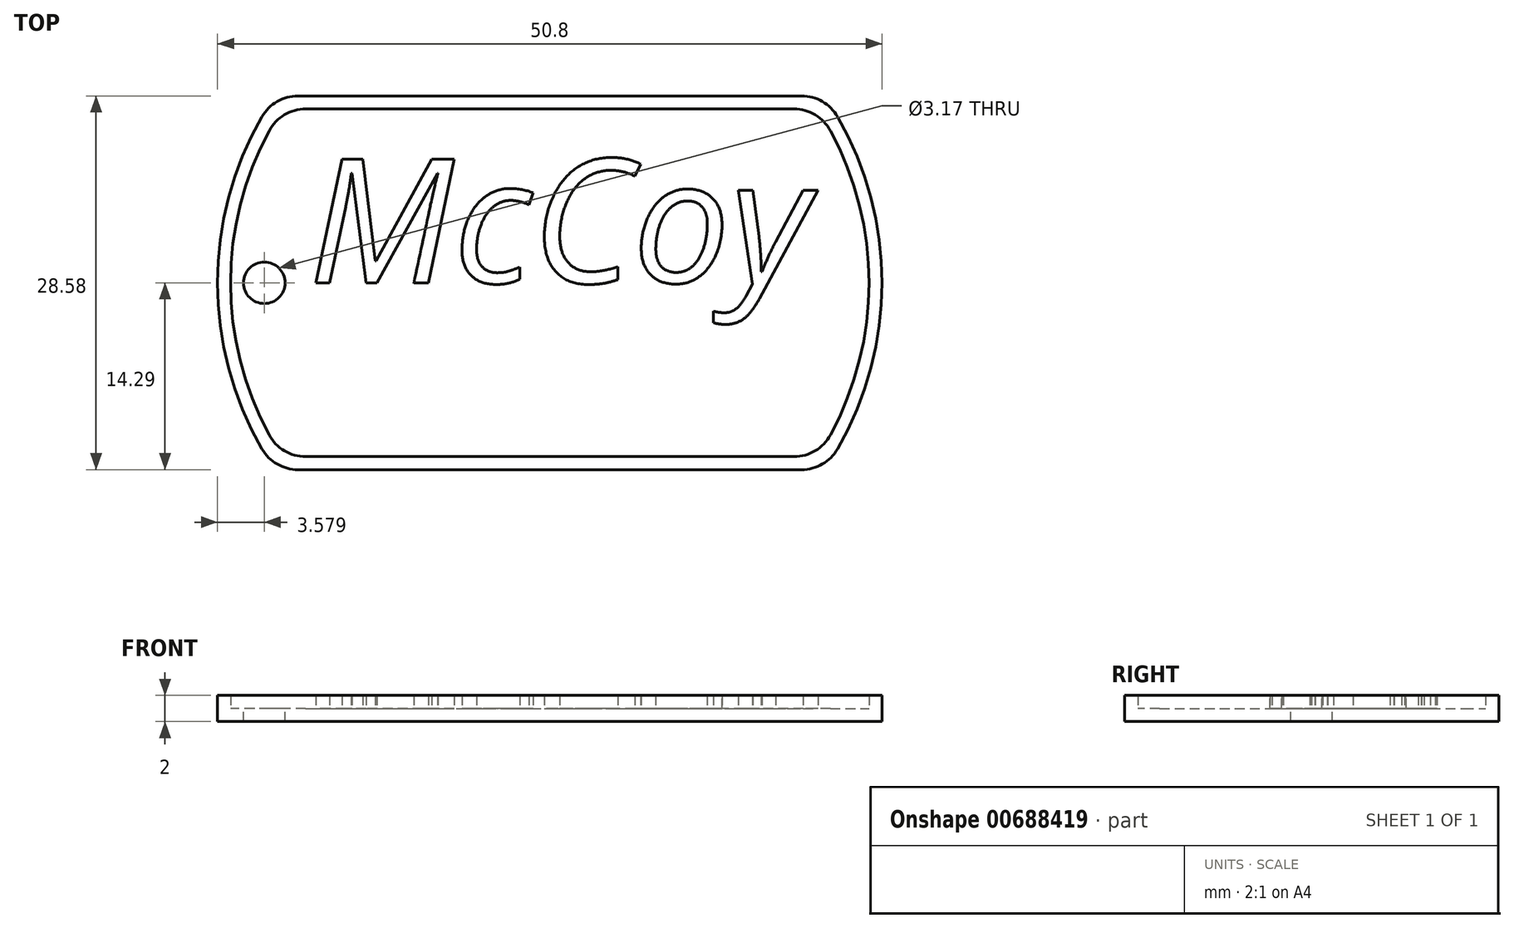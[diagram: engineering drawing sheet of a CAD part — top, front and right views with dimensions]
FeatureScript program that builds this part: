
annotation { "Feature Type Name" : "Feature", "Feature Type Description" : "" }
export const myFeature = defineFeature(function(context is Context, id is Id, definition is map)
    precondition{}
    {
        {
            var Q0;
            Q0=qCreatedBy(makeId("Top.planeOp"),FACE);
            var sketch = newSketch(context, id + "F0", { "sketchPlane" : qUnion([Q0])});
            skArc(sketch, "E0", {"start": v(-22, 12.7) * mm, "mid": v(-25.4, 0) * mm, "end": v(-22, -12.7) * mm});
            skLineSegment(sketch, "E1.top", {"start": v(-19.25, -14.29) * mm, "end": v(19.25, -14.29) * mm});
            skArc(sketch, "E2.trimOffspring", {"start": v(22, -12.7) * mm, "mid": v(25.4, 0) * mm, "end": v(22, 12.7) * mm});
            skLineSegment(sketch, "E3", {"start": v(-19.25, 14.29) * mm, "end": v(19.25, 14.29) * mm});
            skPoint(sketch, "E4.visualSharp", {"position": v(-21, 14.29) * mm});
            skArc(sketch, "E4.filletArc", {"start": v(-19.25, 14.29) * mm, "mid": v(-20.83, 13.86) * mm, "end": v(-22, 12.7) * mm});
            skPoint(sketch, "E5.visualSharp", {"position": v(21, 14.29) * mm});
            skArc(sketch, "E5.filletArc", {"start": v(22, 12.7) * mm, "mid": v(20.83, 13.86) * mm, "end": v(19.25, 14.29) * mm});
            skPoint(sketch, "E6.visualSharp", {"position": v(21, -14.29) * mm});
            skArc(sketch, "E6.filletArc", {"start": v(19.25, -14.29) * mm, "mid": v(20.83, -13.86) * mm, "end": v(22, -12.7) * mm});
            skPoint(sketch, "E7.visualSharp", {"position": v(-21, -14.29) * mm});
            skArc(sketch, "E7.filletArc", {"start": v(-22, -12.7) * mm, "mid": v(-20.83, -13.86) * mm, "end": v(-19.25, -14.29) * mm});
            skSolve(sketch);
        }
        {
            var Q0;
            Q0=makeQuery(id+"F0.imprint","IMPRINT",FACE,{"disambiguationData":[TD([[makeQuery(id+"F0.imprint","IMPRINT",EDGE,{"derivedFrom":sQuery(id+"F0.wireOp",EDGE,"E0")}),1.0]])]});
            extrude(context, id + "F1", {"entities" : qUnion([Q0]), "depth" : 1 * mm, "offsetDistance" : 25.4 * mm});
        }
        {
            var Q0;
            Q0=makeQuery(id+"F1.opExtrude","CAP_FACE",FACE,{"disambiguationData":[OSD([sQuery(id+"F0.wireOp",EDGE,"E0"),sQuery(id+"F0.wireOp",EDGE,"E1.top"),sQuery(id+"F0.wireOp",EDGE,"E2.trimOffspring"),sQuery(id+"F0.wireOp",EDGE,"E3"),sQuery(id+"F0.wireOp",EDGE,"E4.filletArc"),sQuery(id+"F0.wireOp",EDGE,"E5.filletArc"),sQuery(id+"F0.wireOp",EDGE,"E6.filletArc"),sQuery(id+"F0.wireOp",EDGE,"E7.filletArc")])],"isStart":false});
            var sketch = newSketch(context, id + "F2", { "sketchPlane" : qUnion([Q0])});
            skLineSegment(sketch, "E8.0", {"start": v(-18.66, 13.29) * mm, "end": v(18.66, 13.29) * mm});
            skArc(sketch, "E8.1", {"start": v(-21.45, 11.63) * mm, "mid": v(-24.4, 0) * mm, "end": v(-21.45, -11.63) * mm});
            skLineSegment(sketch, "E8.2", {"start": v(-18.66, -13.29) * mm, "end": v(18.66, -13.29) * mm});
            skArc(sketch, "E8.3", {"start": v(21.45, -11.63) * mm, "mid": v(24.4, 0) * mm, "end": v(21.45, 11.63) * mm});
            skPoint(sketch, "E9.visualSharp", {"position": v(-20.46, 13.29) * mm});
            skArc(sketch, "E9.filletArc", {"start": v(-18.66, 13.29) * mm, "mid": v(-20.29, 12.84) * mm, "end": v(-21.45, 11.63) * mm});
            skPoint(sketch, "E10.visualSharp", {"position": v(20.46, 13.29) * mm});
            skArc(sketch, "E10.filletArc", {"start": v(21.45, 11.63) * mm, "mid": v(20.29, 12.84) * mm, "end": v(18.66, 13.29) * mm});
            skPoint(sketch, "E11.visualSharp", {"position": v(20.46, -13.29) * mm});
            skArc(sketch, "E11.filletArc", {"start": v(18.66, -13.29) * mm, "mid": v(20.29, -12.84) * mm, "end": v(21.45, -11.63) * mm});
            skPoint(sketch, "E12.visualSharp", {"position": v(-20.46, -13.29) * mm});
            skArc(sketch, "E12.filletArc", {"start": v(-21.45, -11.63) * mm, "mid": v(-20.29, -12.84) * mm, "end": v(-18.66, -13.29) * mm});
            skLineSegment(sketch, "E13.0", {"start": v(-19.25, 14.29) * mm, "end": v(19.25, 14.29) * mm});
            skArc(sketch, "E13.1", {"start": v(-22, 12.7) * mm, "mid": v(-25.4, 0) * mm, "end": v(-22, -12.7) * mm});
            skLineSegment(sketch, "E13.2", {"start": v(-19.25, -14.29) * mm, "end": v(19.25, -14.29) * mm});
            skArc(sketch, "E13.3", {"start": v(22, -12.7) * mm, "mid": v(25.4, 0) * mm, "end": v(22, 12.7) * mm});
            skPoint(sketch, "E14.visualSharp", {"position": v(-21, -14.29) * mm});
            skArc(sketch, "E14.filletArc", {"start": v(-22, -12.7) * mm, "mid": v(-20.83, -13.86) * mm, "end": v(-19.25, -14.29) * mm});
            skPoint(sketch, "E15.visualSharp", {"position": v(21, -14.29) * mm});
            skArc(sketch, "E15.filletArc", {"start": v(19.25, -14.29) * mm, "mid": v(20.83, -13.86) * mm, "end": v(22, -12.7) * mm});
            skPoint(sketch, "E16.visualSharp", {"position": v(21, 14.29) * mm});
            skArc(sketch, "E16.filletArc", {"start": v(22, 12.7) * mm, "mid": v(20.83, 13.86) * mm, "end": v(19.25, 14.29) * mm});
            skPoint(sketch, "E17.visualSharp", {"position": v(-21, 14.29) * mm});
            skArc(sketch, "E17.filletArc", {"start": v(-19.25, 14.29) * mm, "mid": v(-20.83, 13.86) * mm, "end": v(-22, 12.7) * mm});
            skSolve(sketch);
        }
        {
            var Q0;
            Q0=makeQuery(id+"F2.imprint","IMPRINT",FACE,{"disambiguationData":[TD([[makeQuery(id+"F2.imprint","IMPRINT",EDGE,{"derivedFrom":sQuery(id+"F2.wireOp",EDGE,"E8.0")}),1.0]])]});
            extrude(context, id + "F3", {"entities" : qUnion([Q0]), "operationType" : NewBodyOperationType.ADD, "depth" : 1 * mm, "offsetDistance" : 25.4 * mm});
        }
        {
            var Q0;
            Q0=makeQuery(id+"F1.opExtrude","CAP_FACE",FACE,{"disambiguationData":[OSD([sQuery(id+"F0.wireOp",EDGE,"E0"),sQuery(id+"F0.wireOp",EDGE,"E1.top"),sQuery(id+"F0.wireOp",EDGE,"E2.trimOffspring"),sQuery(id+"F0.wireOp",EDGE,"E3"),sQuery(id+"F0.wireOp",EDGE,"E4.filletArc"),sQuery(id+"F0.wireOp",EDGE,"E5.filletArc"),sQuery(id+"F0.wireOp",EDGE,"E6.filletArc"),sQuery(id+"F0.wireOp",EDGE,"E7.filletArc")])],"isStart":false});
            var sketch = newSketch(context, id + "F4", { "sketchPlane" : qUnion([Q0])});
            skCircle(sketch, "E18", {"center": v(-21.82, 0) * mm, "radius": 1.59 * mm});
            skSolve(sketch);
        }
        {
            var Q0;
            Q0=makeQuery(id+"F4.imprint","IMPRINT",FACE,{"disambiguationData":[TD([[makeQuery(id+"F4.imprint","IMPRINT",EDGE,{"derivedFrom":sQuery(id+"F4.wireOp",EDGE,"E18")}),1.0]])]});
            extrude(context, id + "F5", {"entities" : qUnion([Q0]), "operationType" : NewBodyOperationType.REMOVE, "oppositeDirection" : true, "depth" : 1 * mm, "offsetDistance" : 25.4 * mm});
        }
        {
            var Q0;
            Q0=makeQuery(id+"F2.imprint","IMPRINT",FACE,{"disambiguationData":[TD([[makeQuery(id+"F2.imprint","IMPRINT",EDGE,{"derivedFrom":sQuery(id+"F2.wireOp",EDGE,"E8.0")}),-1.0]])]});
            var sketch = newSketch(context, id + "F6", { "sketchPlane" : qUnion([Q0])});
            skText(sketch, "E19", { "text": "McCoy", "fontName": "OpenSans-Italic.ttf"});
            const initialGuessF6  = {"E19": [-0.01842, 0, 1, 0, 0.00953]};
            skSetInitialGuess(sketch, initialGuessF6);
            skSolve(sketch);
        }
        {
            var Q0;
            Q0 = qSketchRegion(id + "F6", true);
            extrude(context, id + "F7", {"entities" : qUnion([Q0]), "operationType" : NewBodyOperationType.ADD, "depth" : 1 * mm, "offsetDistance" : 25.4 * mm});
        }
    });
